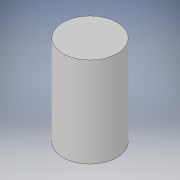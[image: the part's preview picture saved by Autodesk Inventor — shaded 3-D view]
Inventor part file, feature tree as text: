
AUTODESK INVENTOR PART (.ipt)
format: ipt  version: 2019 (Build 230136000, 136)  size: 88,064 bytes
history: native  units: mm
features: extrude x1, sketch x1
ambient origin geometry x8: Origin, YZ Plane, XZ Plane, XY Plane, X Axis, Y Axis, Z Axis, Center Point
bodies: Solid1 (feature_tree)
feature tree (2):
  extrude  "Extrusion1"  Depth=100.0mm TaperAngle=0.0deg
  sketch  "Sketch1"  dims[d0=60.0mm d1=100.0mm d2=0.0mm]
